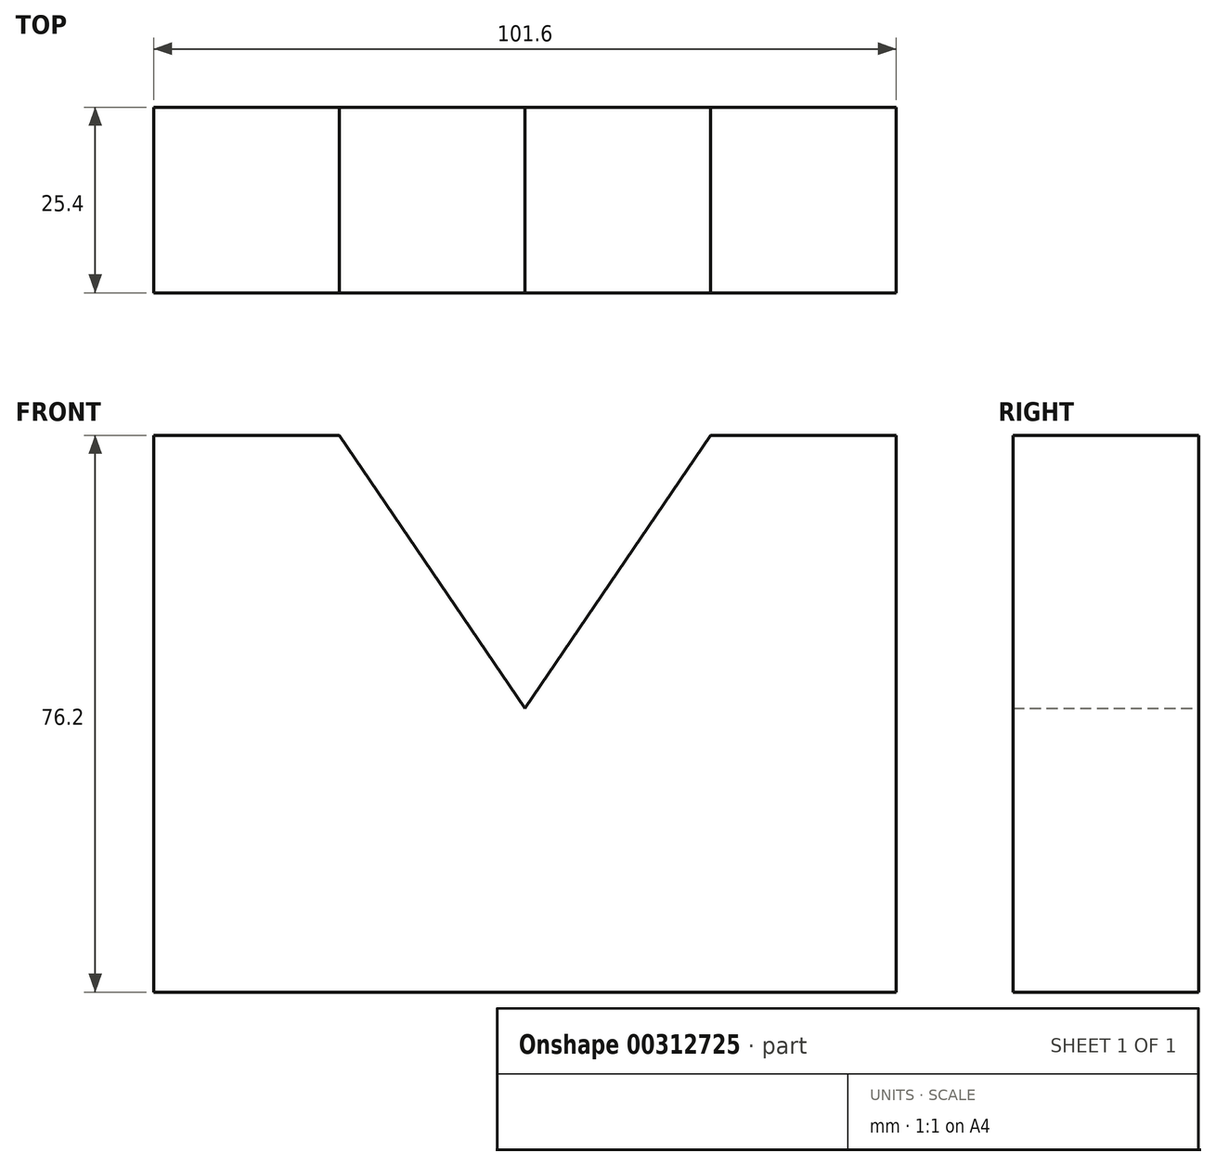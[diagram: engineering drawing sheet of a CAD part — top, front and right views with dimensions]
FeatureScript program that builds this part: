
annotation { "Feature Type Name" : "Feature", "Feature Type Description" : "" }
export const myFeature = defineFeature(function(context is Context, id is Id, definition is map)
    precondition{}
    {
        {
            var Q0;
            Q0=qCreatedBy(makeId("Front.planeOp"),FACE);
            var sketch = newSketch(context, id + "F0", { "sketchPlane" : qUnion([Q0])});
            skLineSegment(sketch, "E0", {"start": v(38.46, 27.73) * mm, "end": v(38.46, -48.47) * mm});
            skLineSegment(sketch, "E1", {"start": v(38.46, -48.47) * mm, "end": v(-63.14, -48.47) * mm});
            skLineSegment(sketch, "E2", {"start": v(-63.14, -48.47) * mm, "end": v(-63.14, 27.73) * mm});
            skLineSegment(sketch, "E3", {"start": v(-63.14, 27.73) * mm, "end": v(-37.74, 27.73) * mm});
            skLineSegment(sketch, "E4", {"start": v(38.46, 27.73) * mm, "end": v(13.06, 27.73) * mm});
            skLineSegment(sketch, "E5", {"start": v(13.06, 27.73) * mm, "end": v(-12.34, -9.65) * mm});
            skLineSegment(sketch, "E6", {"start": v(-12.34, -9.65) * mm, "end": v(-37.74, 27.73) * mm});
            skPoint(sketch, "E7", {"position": v(-12.34, -48.47) * mm});
            skLineSegment(sketch, "E8", {"start": v(-12.34, -48.47) * mm, "end": v(-12.34, -47.75) * mm});
            skSolve(sketch);
        }
        {
            var Q0;
            {var subQ3=sQuery(id+"F0.wireOp",EDGE,"E0");Q0=makeQuery(id+"F0.imprint","IMPRINT",FACE,{"disambiguationData":[TD([[makeQuery(id+"F0.imprint","IMPRINT",EDGE,{"derivedFrom":subQ3}),-1.0]])]});}
            extrude(context, id + "F1", {"entities" : qUnion([Q0]), "depth" : 25.4 * mm});
        }
    });
